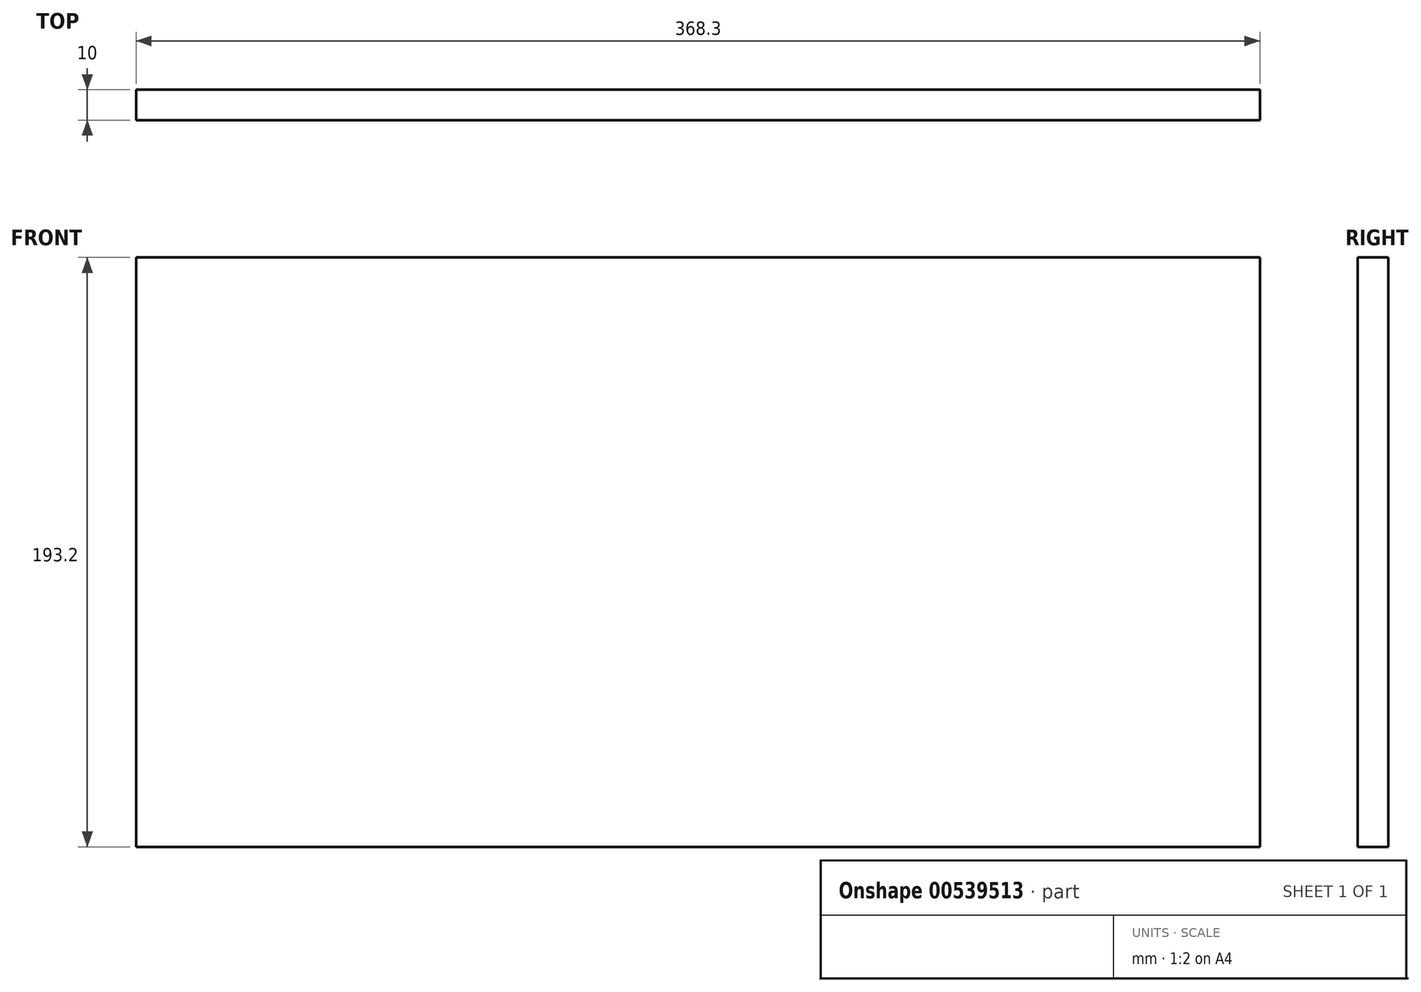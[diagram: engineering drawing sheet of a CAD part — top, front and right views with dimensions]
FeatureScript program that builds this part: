
annotation { "Feature Type Name" : "Feature", "Feature Type Description" : "" }
export const myFeature = defineFeature(function(context is Context, id is Id, definition is map)
    precondition{}
    {
        {
            var Q0;
            Q0=qCreatedBy(makeId("Front.planeOp"),FACE);
            var sketch = newSketch(context, id + "F0", { "sketchPlane" : qUnion([Q0])});
            skLineSegment(sketch, "E0.bottom", {"start": v(184.15, -96.6) * mm, "end": v(-184.15, -96.6) * mm});
            skLineSegment(sketch, "E0.top", {"start": v(184.15, 96.6) * mm, "end": v(-184.15, 96.6) * mm});
            skLineSegment(sketch, "E0.left", {"start": v(184.15, -96.6) * mm, "end": v(184.15, 96.6) * mm});
            skLineSegment(sketch, "E0.right", {"start": v(-184.15, -96.6) * mm, "end": v(-184.15, 96.6) * mm});
            skPoint(sketch, "E0.middle", {"position": v(0, 0) * mm});
            skSolve(sketch);
        }
        {
            var Q0;
            Q0=makeQuery(id+"F0.imprint","IMPRINT",FACE,{"disambiguationData":[TD([[makeQuery(id+"F0.imprint","IMPRINT",EDGE,{"derivedFrom":sQuery(id+"F0.wireOp",EDGE,"E0.bottom")}),-1.0]])]});
            extrude(context, id + "F1", {"entities" : qUnion([Q0]), "depth" : 10 * mm});
        }
    });
